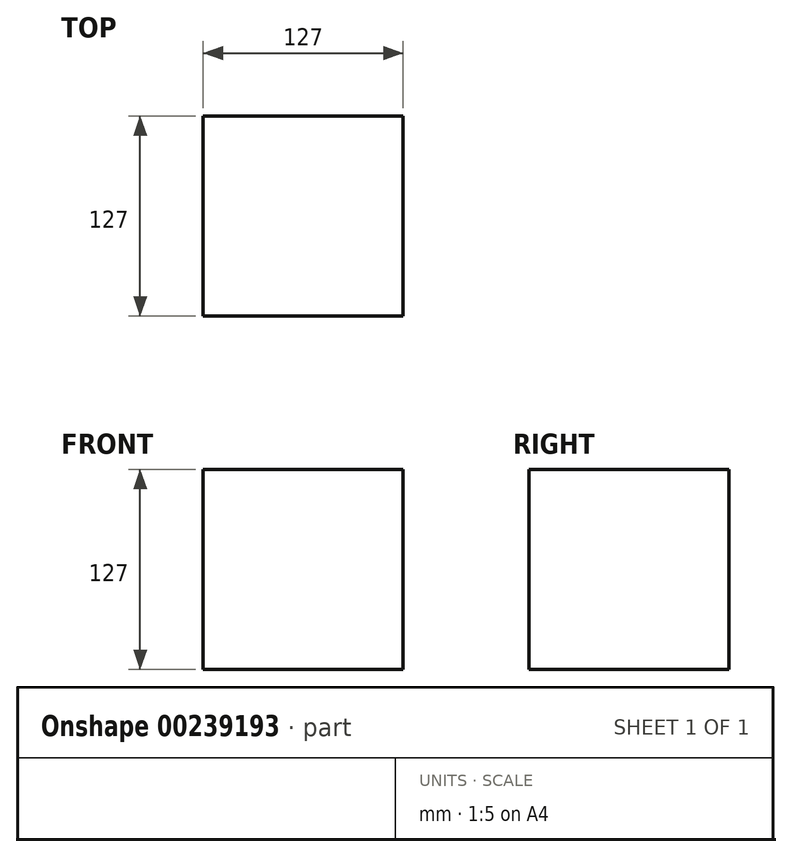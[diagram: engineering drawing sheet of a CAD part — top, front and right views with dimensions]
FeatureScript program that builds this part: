
annotation { "Feature Type Name" : "Feature", "Feature Type Description" : "" }
export const myFeature = defineFeature(function(context is Context, id is Id, definition is map)
    precondition{}
    {
        {
            var Q0;
            Q0=qCreatedBy(makeId("Front.planeOp"),FACE);
            var sketch = newSketch(context, id + "F0", { "sketchPlane" : qUnion([Q0])});
            skLineSegment(sketch, "E0.bottom", {"start": v(-54.3, 72.41) * mm, "end": v(72.7, 72.41) * mm});
            skLineSegment(sketch, "E0.top", {"start": v(-54.3, -54.59) * mm, "end": v(72.7, -54.59) * mm});
            skLineSegment(sketch, "E0.left", {"start": v(-54.3, 72.41) * mm, "end": v(-54.3, -54.59) * mm});
            skLineSegment(sketch, "E0.right", {"start": v(72.7, 72.41) * mm, "end": v(72.7, -54.59) * mm});
            skSolve(sketch);
        }
        {
            var Q0;
            Q0=makeQuery(id+"F0.imprint","IMPRINT",FACE,{"disambiguationData":[TD([[makeQuery(id+"F0.imprint","IMPRINT",EDGE,{"derivedFrom":sQuery(id+"F0.wireOp",EDGE,"E0.bottom")}),-1.0]])]});
            extrude(context, id + "F1", {"entities" : qUnion([Q0]), "depth" : 127 * mm});
        }
    });
